# Revit family: Spray Bodies UNI-Spray Series
name_source: partatom
category: Acessórios do tubo
units: mm (PartAtom-declared; Revit-internal decimal feet)

## family parameters
Com base no plano de trabalho = Não
Compartilhado = Não
Corte com vazios quando carregada = Não
Cota do conector redondo = Utilizar diâmetro
Número OmniClass = 23.60.30.11.14
Sempre na vertical = Sim
Tipo de parte = Normal
Título OmniClass = Pipework Fittings

## types (1)
- UNI-Spray Series
    AA1 = 135.00°
    Black Plastic = Black Plastic
    Body height = 15
    Conection = 2
    DD1 = 1
    DD10 = 3
    DD11 = 0
    DD13 = 2
    DD2 = 1
    DD3 = 3
    DD5 = 2
    DD6 = 2
    DD7 = 1
    DD9 = 1
    DT1 = 1
    DT2 = 1
    DT3 = 1
    DT4 = 1
    DT5 = 0
    DT6 = 2
    DT7 = 3
    DT8 = 0
    Descrição = Spray Bodies UNI-Spray Series - US400 Model
    Elevação padrão = 0
    H1 = 5
    Modelo = US400
    Pop up height = 10
    R1 = 1
    R2 = 3
    R3 = 2
    R4 = 1
    R5 = 1
    RN = 1
    RT = 0
    RainBird: Description = Spray Bodies UNI-Spray Series - US400 Model
    RainBird: Product Link = https://store.rainbird.com
    Side inlet = Não
    SupportProjetos: Level of Detail = LOD 300
    SupportProjetos: Reviw = R01
    SupportProjetos: Reviw Date = 15/11/2020
    URL = https://www.rainbird.com
